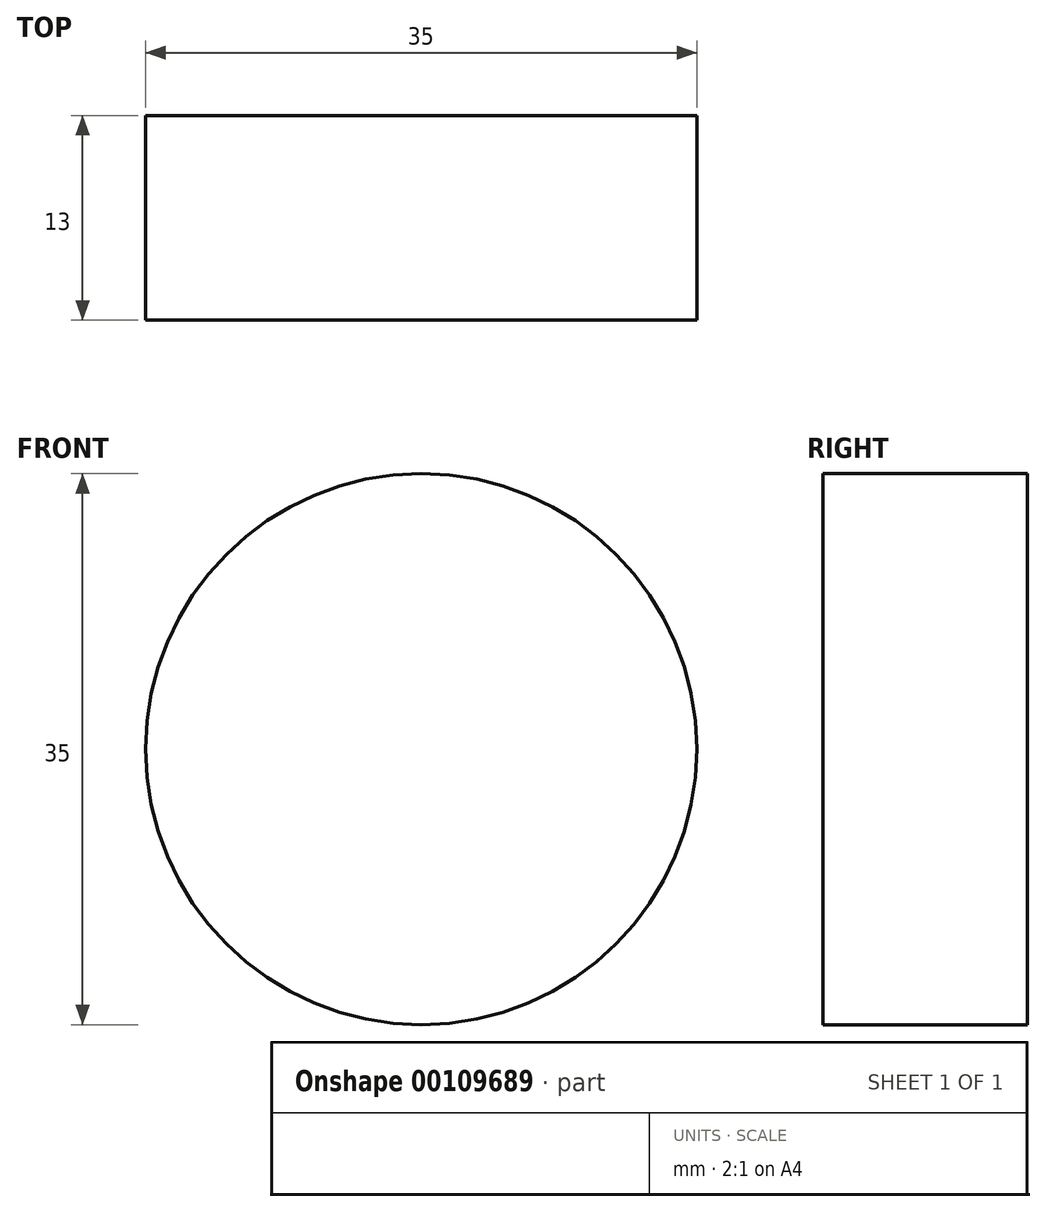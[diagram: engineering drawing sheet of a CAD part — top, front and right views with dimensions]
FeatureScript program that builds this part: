
annotation { "Feature Type Name" : "Feature", "Feature Type Description" : "" }
export const myFeature = defineFeature(function(context is Context, id is Id, definition is map)
    precondition{}
    {
        {
            var Q0;
            Q0=qCreatedBy(makeId("Front.planeOp"),FACE);
            var sketch = newSketch(context, id + "F0", { "sketchPlane" : qUnion([Q0])});
            skCircle(sketch, "E0", {"center": v(0, 0) * mm, "radius": 17.5 * mm});
            skSolve(sketch);
        }
        {
            var Q0;
            Q0=makeQuery(id+"F0.imprint","IMPRINT",FACE,{"disambiguationData":[TD([[makeQuery(id+"F0.imprint","IMPRINT",EDGE,{"derivedFrom":sQuery(id+"F0.wireOp",EDGE,"E0")}),1.0]])]});
            extrude(context, id + "F1", {"entities" : qUnion([Q0]), "depth" : 13 * mm});
        }
    });
